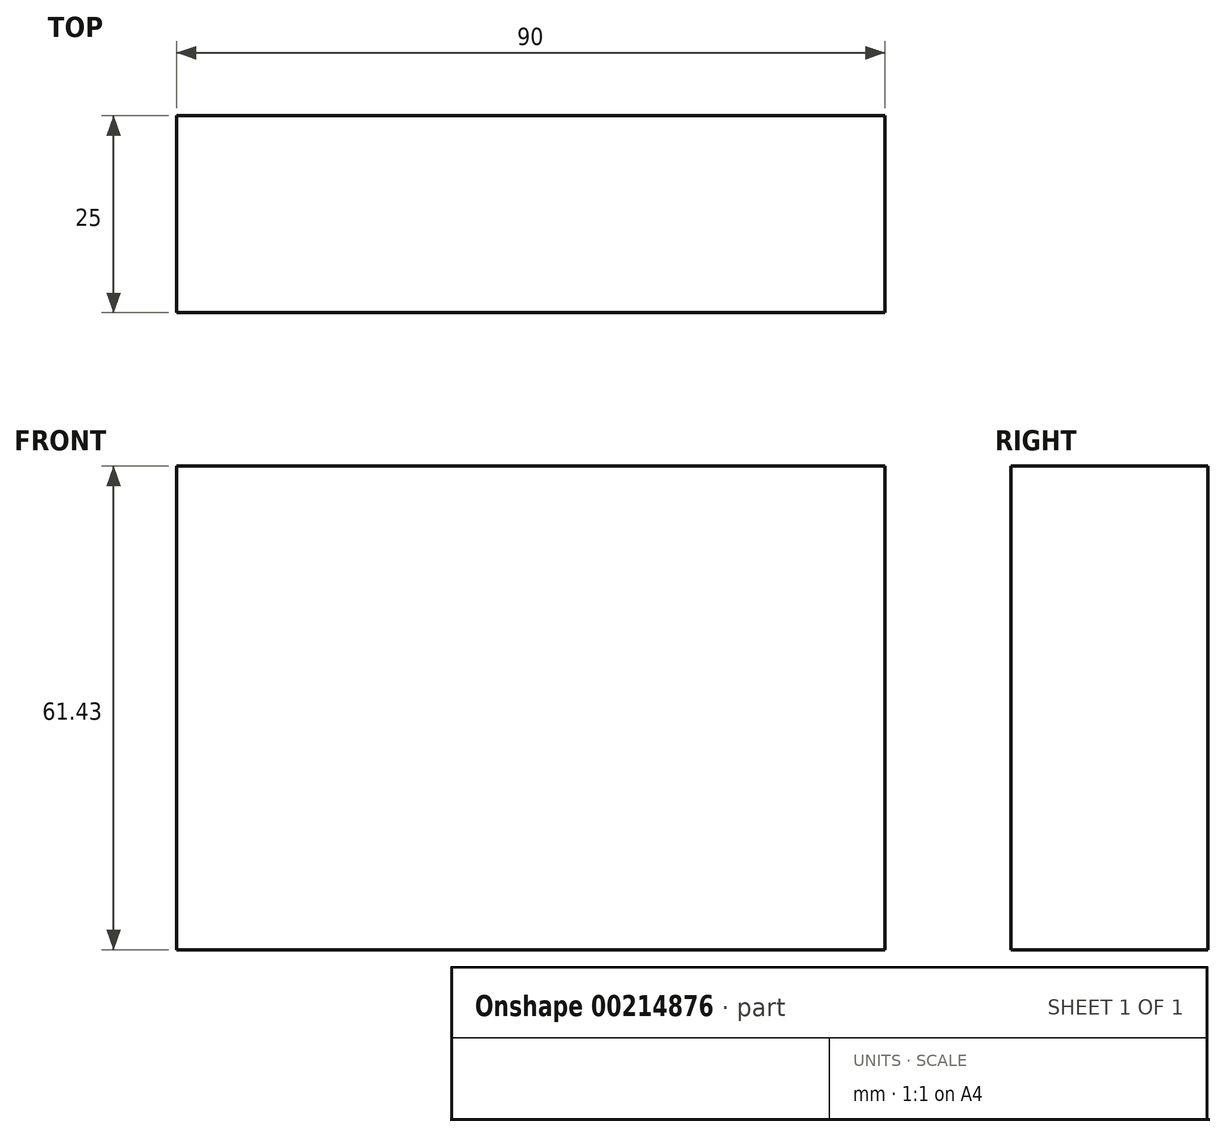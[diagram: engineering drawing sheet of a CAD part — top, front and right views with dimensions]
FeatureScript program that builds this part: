
annotation { "Feature Type Name" : "Feature", "Feature Type Description" : "" }
export const myFeature = defineFeature(function(context is Context, id is Id, definition is map)
    precondition{}
    {
        {
            var Q0;
            Q0=qCreatedBy(makeId("Front.planeOp"),FACE);
            var sketch = newSketch(context, id + "F0", { "sketchPlane" : qUnion([Q0])});
            skLineSegment(sketch, "E0.bottom", {"start": v(-77.33, -16.31) * mm, "end": v(12.67, -16.31) * mm});
            skLineSegment(sketch, "E0.top", {"start": v(-77.33, -77.74) * mm, "end": v(12.67, -77.74) * mm});
            skLineSegment(sketch, "E0.left", {"start": v(-77.33, -16.31) * mm, "end": v(-77.33, -77.74) * mm});
            skLineSegment(sketch, "E0.right", {"start": v(12.67, -16.31) * mm, "end": v(12.67, -77.74) * mm});
            skSolve(sketch);
        }
        {
            var Q0;
            Q0 = qSketchRegion(id + "F0", true);
            extrude(context, id + "F1", {"entities" : qUnion([Q0]), "depth" : 25 * mm});
        }
    });
